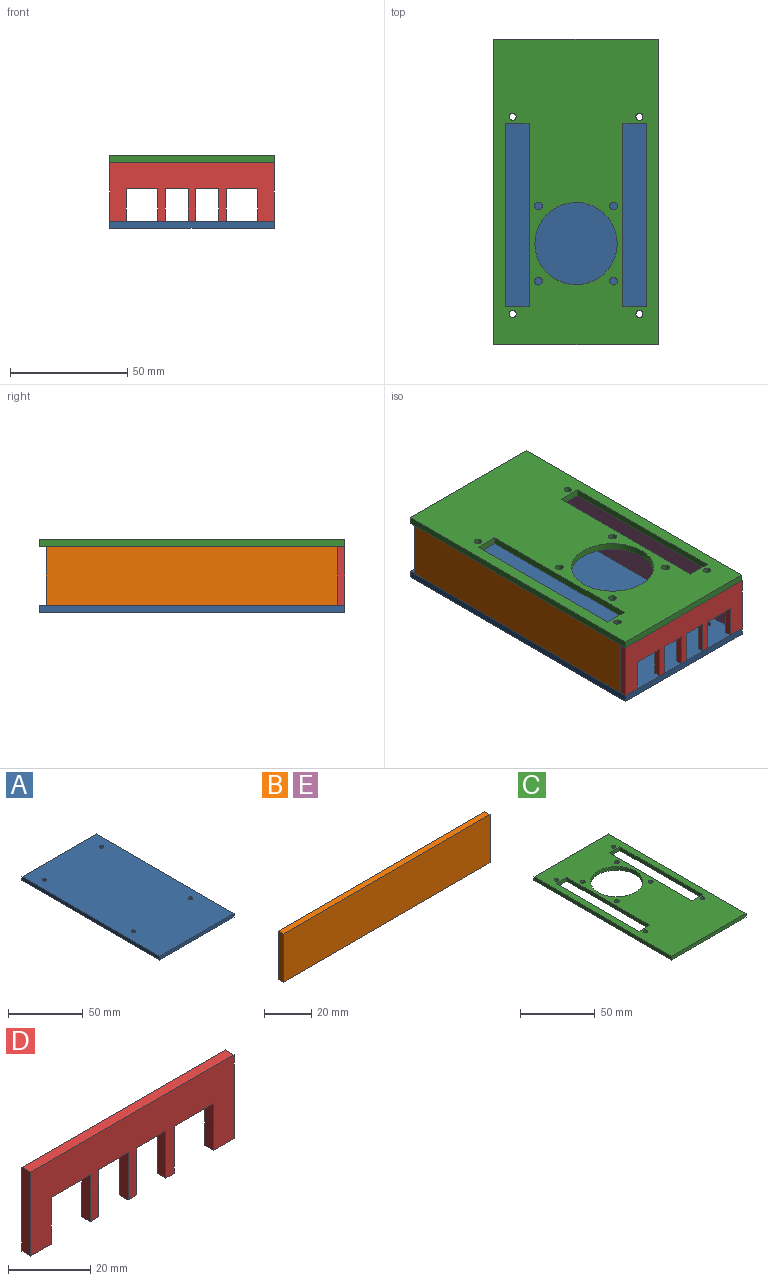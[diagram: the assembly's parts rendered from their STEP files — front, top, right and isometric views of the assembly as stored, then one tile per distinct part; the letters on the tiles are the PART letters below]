
ASSEMBLY  parts=5 mates=13
PART A: 10 faces, bbox 70x130x3 mm
  f0: plane 70x3mm, normal (0,1,0), area 210mm2, adj f1,f3,f4,f5
  f1: plane 130x3mm, normal (-1,0,0), area 390mm2, adj f0,f2,f4,f5
  f2: plane 70x3mm, normal (0,-1,0), area 210mm2, adj f1,f3,f4,f5
  f3: plane 130x3mm, normal (1,0,0), area 390mm2, adj f0,f2,f4,f5
  f4: plane 130x70mm, normal (0,0,1), area 9071.7mm2, adj f0,f1,f2,f3,f6,f7,f8,f9
  f5: plane 130x70mm, normal (0,0,-1), area 9071.7mm2, adj f0,f1,f2,f3,f6,f7,f8,f9
  f6: cylinder r=1.5mm len=3mm, axis (0,0,-1), area 28.3mm2, adj f4,f5
  f7: cylinder r=1.5mm len=3mm, axis (0,0,-1), area 28.3mm2, adj f4,f5
  f8: cylinder r=1.5mm len=3mm, axis (0,0,-1), area 28.3mm2, adj f4,f5
  f9: cylinder r=1.5mm len=3mm, axis (0,0,-1), area 28.3mm2, adj f4,f5
PART B: 6 faces, bbox 124x3x25 mm
  f0: plane 124x3mm, normal (0,0,1), area 372mm2, adj f1,f3,f4,f5
  f1: plane 25x3mm, normal (-1,0,0), area 75mm2, adj f0,f2,f4,f5
  f2: plane 124x3mm, normal (0,0,-1), area 372mm2, adj f1,f3,f4,f5
  f3: plane 25x3mm, normal (1,0,0), area 75mm2, adj f0,f2,f4,f5
  f4: plane 124x25mm, normal (0,-1,0), area 3100mm2, adj f0,f1,f2,f3
  f5: plane 124x25mm, normal (0,1,0), area 3100mm2, adj f0,f1,f2,f3
PART C: 23 faces, bbox 70x130x3 mm
  f0: plane 130x70mm, normal (0,0,1), area 6515.4mm2, adj f2,f3,f4,f5,f6,f7,f8,f9
  f1: plane 130x70mm, normal (0,0,-1), area 6515.4mm2, adj f2,f3,f4,f5,f6,f7,f8,f9
  f2: plane 70x3mm, normal (0,1,0), area 210mm2, adj f0,f1,f3,f5
  f3: plane 130x3mm, normal (-1,0,0), area 390mm2, adj f0,f1,f2,f4
  f4: plane 70x3mm, normal (0,-1,0), area 210mm2, adj f0,f1,f3,f5
  f5: plane 130x3mm, normal (1,0,0), area 390mm2, adj f0,f1,f2,f4
  f6: cylinder r=1.5mm len=3mm, axis (0,0,-1), area 28.3mm2, adj f0,f1
  f7: cylinder r=1.65mm len=3.3mm, axis (0,0,-1), area 31.1mm2, adj f0,f1
  f8: cylinder r=1.65mm len=3.3mm, axis (0,0,-1), area 31.1mm2, adj f0,f1
  f9: cylinder r=1.65mm len=3.3mm, axis (0,0,-1), area 31.1mm2, adj f0,f1
  f10: cylinder r=1.65mm len=3.3mm, axis (0,0,-1), area 31.1mm2, adj f0,f1
  f11: cylinder r=17.5mm len=35mm, axis (0,0,-1), area 329.9mm2, adj f0,f1
  f12: cylinder r=1.5mm len=3mm, axis (0,0,-1), area 28.3mm2, adj f0,f1
  f13: cylinder r=1.5mm len=3mm, axis (0,0,-1), area 28.3mm2, adj f0,f1
  f14: cylinder r=1.5mm len=3mm, axis (0,0,-1), area 28.3mm2, adj f0,f1
  f15: plane 78x3mm, normal (1,0,0), area 234mm2, adj f0,f1,f16,f17
  f16: plane 10x3mm, normal (0,1,0), area 30mm2, adj f0,f1,f15,f18
  f17: plane 10x3mm, normal (0,-1,0), area 30mm2, adj f0,f1,f15,f18
  f18: plane 78x3mm, normal (-1,0,0), area 234mm2, adj f0,f1,f16,f17
  f19: plane 10x3mm, normal (0,-1,0), area 30mm2, adj f0,f1,f20,f21
  f20: plane 78x3mm, normal (1,0,0), area 234mm2, adj f0,f1,f19,f22
  f21: plane 78x3mm, normal (-1,0,0), area 234mm2, adj f0,f1,f19,f22
  f22: plane 10x3mm, normal (0,1,0), area 30mm2, adj f0,f1,f20,f21
PART D: 22 faces, bbox 70x3x25 mm
  f0: plane 7x3mm, normal (0,0,-1), area 21mm2, adj f4,f6,f9,f19
  f1: plane 3x3mm, normal (0,0,-1), area 9mm2, adj f4,f9,f16,f20
  f2: plane 3x3mm, normal (0,0,-1), area 9mm2, adj f4,f9,f13,f17
  f3: plane 3x3mm, normal (0,0,-1), area 9mm2, adj f4,f9,f10,f14
  f4: plane 70x25mm, normal (0,1,0), area 1092mm2, adj f0,f1,f2,f3,f5,f6,f7,f8
  f5: plane 70x3mm, normal (0,0,1), area 210mm2, adj f4,f6,f8,f9
  f6: plane 25x3mm, normal (-1,0,0), area 75mm2, adj f0,f4,f5,f9
  f7: plane 7x3mm, normal (0,0,-1), area 21mm2, adj f4,f8,f9,f11
  f8: plane 25x3mm, normal (1,0,0), area 75mm2, adj f4,f5,f7,f9
  f9: plane 70x25mm, normal (0,-1,0), area 1092mm2, adj f0,f1,f2,f3,f5,f6,f7,f8
  f10: plane 14x3mm, normal (1,0,0), area 42mm2, adj f3,f4,f9,f12
  f11: plane 14x3mm, normal (-1,0,0), area 42mm2, adj f4,f7,f9,f12
  f12: plane 13.5x3mm, normal (0,0,-1), area 40.5mm2, adj f4,f9,f10,f11
  f13: plane 14x3mm, normal (1,0,0), area 42mm2, adj f2,f4,f9,f15
  f14: plane 14x3mm, normal (-1,0,0), area 42mm2, adj f3,f4,f9,f15
  f15: plane 10x3mm, normal (0,0,-1), area 30mm2, adj f4,f9,f13,f14
  f16: plane 14x3mm, normal (1,0,0), area 42mm2, adj f1,f4,f9,f18
  f17: plane 14x3mm, normal (-1,0,0), area 42mm2, adj f2,f4,f9,f18
  f18: plane 10x3mm, normal (0,0,-1), area 30mm2, adj f4,f9,f16,f17
  f19: plane 14x3mm, normal (1,0,0), area 42mm2, adj f0,f4,f9,f21
  f20: plane 14x3mm, normal (-1,0,0), area 42mm2, adj f1,f4,f9,f21
  f21: plane 13.5x3mm, normal (0,0,-1), area 40.5mm2, adj f4,f9,f19,f20
PART E: same geometry as B
PLACE A rot(axis=(1,0,0),180deg) t=(2.09,48.07,16.54)mm
PLACE B rot(axis=(0,0,-1),90deg) t=(-29.91,48.07,29.04)mm
PLACE C rot(axis=(0,0,1),180deg) t=(2.09,48.07,41.54)mm
PLACE D t=(2.09,-13.93,29.04)mm
PLACE E rot(axis=(0,0,1),90deg) t=(34.09,48.07,29.04)mm
MATE planar C.f2 <-> A.f0  axis (0,-1,0) through (2.09,-16.93,43.04)mm
MATE planar D.f9 <-> A.f0  axis (0,-1,0) through (2.09,-16.93,32.36)mm
MATE planar D.f0 <-> A.f5  axis (0,0,-1) through (-29.41,-15.43,16.54)mm
MATE planar E.f1 <-> D.f4  axis (0,-1,0) through (34.09,-13.93,29.04)mm
MATE planar C.f1 <-> D.f5  axis (0,0,-1) through (2.09,53.87,41.54)mm
MATE planar D.f8 <-> A.f3  axis (1,0,0) through (37.09,-15.43,29.04)mm
MATE planar C.f5 <-> A.f1  axis (-1,0,0) through (-32.91,113.07,43.04)mm
MATE planar A.f5 <-> E.f2  axis (0,0,1) through (2.09,48.1,16.54)mm
MATE planar B.f3 <-> E.f1  axis (0,-1,0) through (-29.91,-13.93,41.54)mm
MATE planar E.f4 <-> A.f3  axis (1,0,0) through (37.09,-13.93,29.04)mm
MATE planar B.f4 <-> A.f1  axis (-1,0,0) through (-32.91,48.07,29.04)mm
MATE planar C.f3 <-> A.f3  axis (1,0,0) through (37.09,48.07,43.04)mm
MATE planar A.f5 <-> B.f2  axis (0,0,1) through (2.09,48.1,16.54)mm
